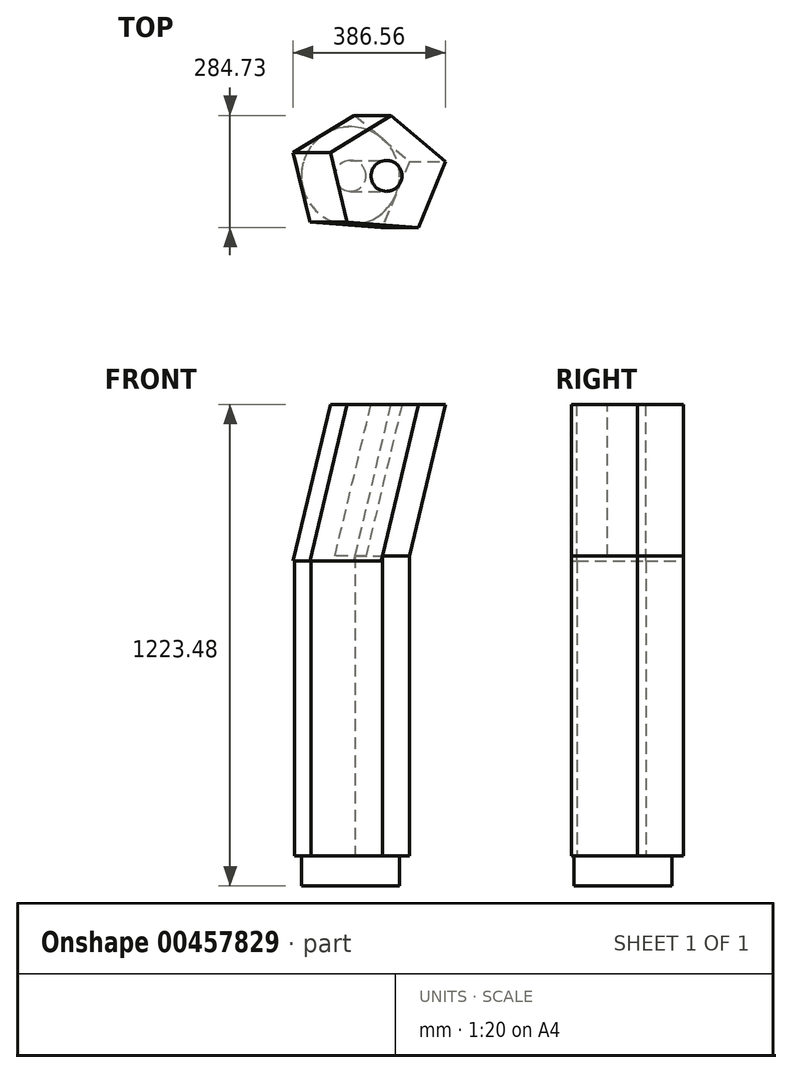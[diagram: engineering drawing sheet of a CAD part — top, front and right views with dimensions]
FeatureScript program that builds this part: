
annotation { "Feature Type Name" : "Feature", "Feature Type Description" : "" }
export const myFeature = defineFeature(function(context is Context, id is Id, definition is map)
    precondition{}
    {
        {
            var Q0;
            Q0=qCreatedBy(makeId("Top.planeOp"),FACE);
            var sketch = newSketch(context, id + "F0", { "sketchPlane" : qUnion([Q0])});
            skCircle(sketch, "E0", {"center": v(0, 0) * mm, "radius": 124.63 * mm});
            skSolve(sketch);
        }
        {
            var Q0;
            Q0 = qSketchRegion(id + "F0", true);
            extrude(context, id + "F1", {"entities" : qUnion([Q0]), "depth" : 76.2 * mm});
        }
        {
            var Q0;
            Q0=makeQuery(id+"F1.opExtrude","CAP_FACE",FACE,{"disambiguationData":[OSD([sQuery(id+"F0.wireOp",EDGE,"E0")])],"isStart":false});
            var sketch = newSketch(context, id + "F2", { "sketchPlane" : qUnion([Q0])});
            skCircle(sketch, "E1.cCircle", {"center": v(0, 0) * mm, "radius": 124.63 * mm, "construction": true});
            skLineSegment(sketch, "E1.0", {"start": v(80.84, -131.13) * mm, "end": v(-99.73, -117.4) * mm});
            skLineSegment(sketch, "E1.1", {"start": v(-99.73, -117.4) * mm, "end": v(-142.48, 58.57) * mm});
            skLineSegment(sketch, "E1.2", {"start": v(-142.48, 58.57) * mm, "end": v(11.67, 153.6) * mm});
            skLineSegment(sketch, "E1.3", {"start": v(11.67, 153.6) * mm, "end": v(149.7, 36.36) * mm});
            skLineSegment(sketch, "E1.4", {"start": v(149.7, 36.36) * mm, "end": v(80.84, -131.13) * mm});
            skPoint(sketch, "E1.0.midPoint", {"position": v(-9.44, -124.27) * mm});
            skSolve(sketch);
        }
        {
            var Q0;
            Q0 = qSketchRegion(id + "F2", true);
            extrude(context, id + "F3", {"entities" : qUnion([Q0]), "operationType" : NewBodyOperationType.ADD, "depth" : 762 * mm});
        }
        {
            var Q0;
            Q0=qCreatedBy(makeId("Front.planeOp"),FACE);
            var sketch = newSketch(context, id + "F4", { "sketchPlane" : qUnion([Q0])});
            skLineSegment(sketch, "E2", {"start": v(0, 826.17) * mm, "end": v(94.38, 1223.48) * mm});
            skSolve(sketch);
        }
        {
            var Q0;
            Q0=makeQuery(id+"F3.opExtrude","CAP_FACE",FACE,{"disambiguationData":[OSD([sQuery(id+"F2.wireOp",EDGE,"E1.0"),sQuery(id+"F2.wireOp",EDGE,"E1.1"),sQuery(id+"F2.wireOp",EDGE,"E1.2"),sQuery(id+"F2.wireOp",EDGE,"E1.3"),sQuery(id+"F2.wireOp",EDGE,"E1.4")])],"isStart":false});
            var sketch = newSketch(context, id + "F5", { "sketchPlane" : qUnion([Q0])});
            skSolve(sketch);
        }
        {
            var Q0;
            Q0=makeQuery(id+"F5.imprint","IMPRINT",FACE,{"disambiguationData":[TD([[makeQuery(id+"F5.imprint","IMPRINT",EDGE,{"derivedFrom":makeQuery(id+"F3.opExtrude","CAP_EDGE",EDGE,{"disambiguationData":[OSD([sQuery(id+"F2.wireOp",EDGE,"E1.0")])],"isStart":false})}),-1.0]])]});
            var sketch = newSketch(context, id + "F6", { "sketchPlane" : qUnion([Q0])});
            skCircle(sketch, "E3", {"center": v(0, 0) * mm, "radius": 39.34 * mm});
            skSolve(sketch);
        }
        {
            var Q0;
            Q0=makeQuery(id+"F6.imprint","IMPRINT",FACE,{"disambiguationData":[TD([[makeQuery(id+"F6.imprint","IMPRINT",EDGE,{"derivedFrom":sQuery(id+"F6.wireOp",EDGE,"E3")}),-1.0]])]});
            var Q1;
            Q1=sQuery(id+"F4.wireOp",EDGE,"E2");
            sweep(context, id + "F7", {"operationType" : NewBodyOperationType.ADD, "profiles" : qUnion([Q0]), "path" : qUnion([Q1])});
        }
    });
